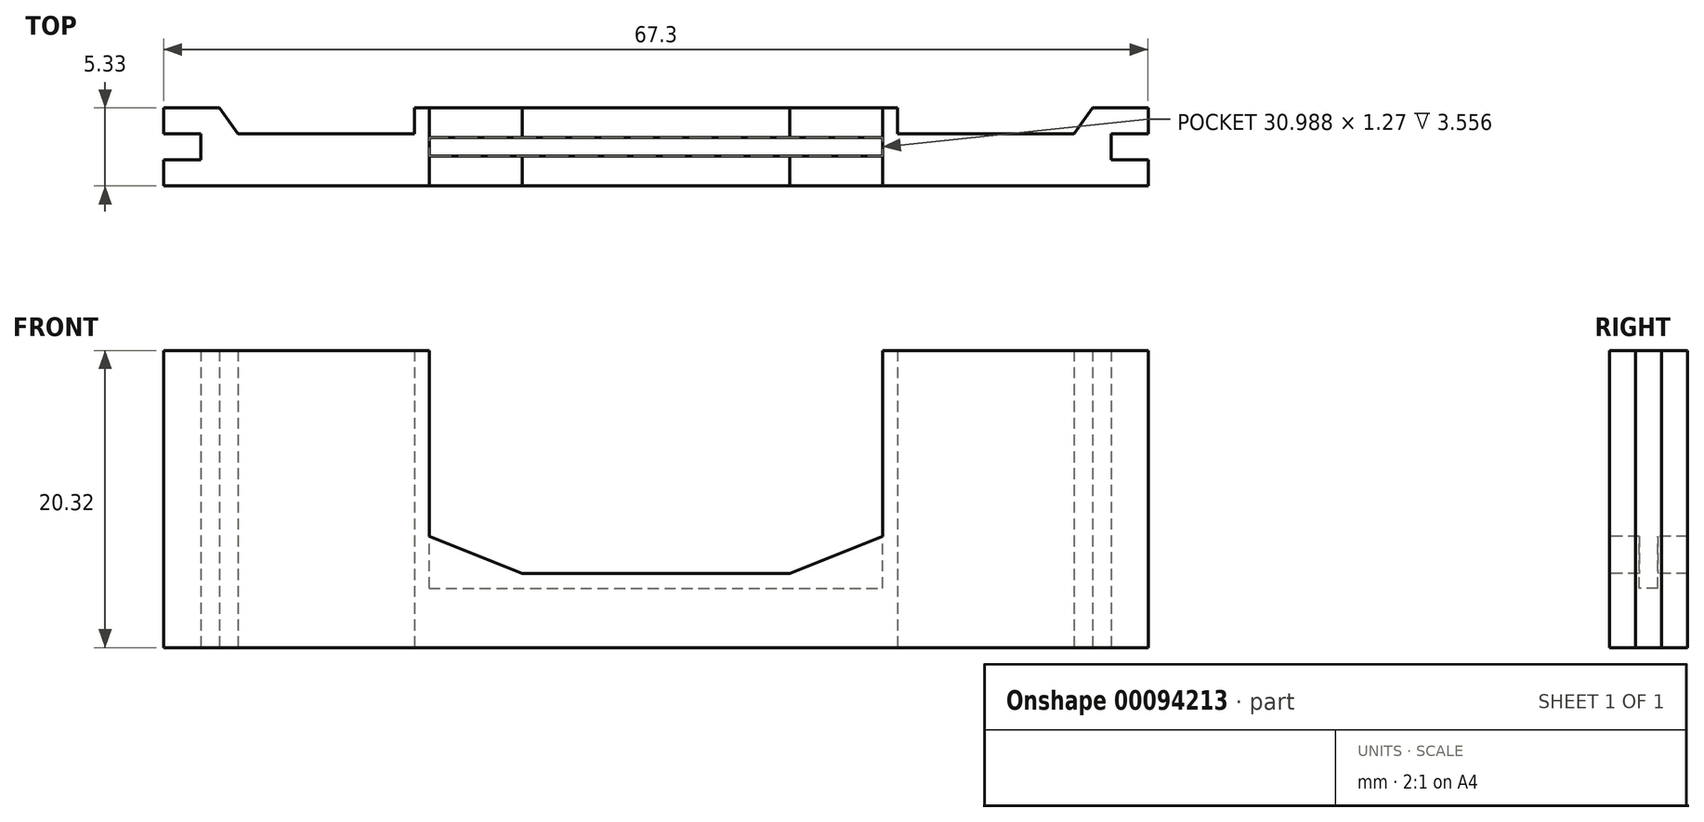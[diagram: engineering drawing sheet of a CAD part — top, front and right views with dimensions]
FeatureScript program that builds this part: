
annotation { "Feature Type Name" : "Feature", "Feature Type Description" : "" }
export const myFeature = defineFeature(function(context is Context, id is Id, definition is map)
    precondition{}
    {
        {
            var Q0;
            Q0=qCreatedBy(makeId("Top.planeOp"),FACE);
            var sketch = newSketch(context, id + "F0", { "sketchPlane" : qUnion([Q0])});
            skLineSegment(sketch, "E0", {"start": v(-33.66, 1.78) * mm, "end": v(-31.12, 1.78) * mm});
            skLineSegment(sketch, "E1", {"start": v(-31.12, 1.78) * mm, "end": v(-31.12, 3.56) * mm});
            skLineSegment(sketch, "E2", {"start": v(-31.12, 3.56) * mm, "end": v(-33.66, 3.56) * mm});
            skLineSegment(sketch, "E3", {"start": v(-33.66, 3.56) * mm, "end": v(-33.66, 5.33) * mm});
            skLineSegment(sketch, "E4", {"start": v(-33.66, 5.33) * mm, "end": v(-29.85, 5.33) * mm});
            skLineSegment(sketch, "E5", {"start": v(-16.51, 3.56) * mm, "end": v(-16.51, 5.33) * mm});
            skLineSegment(sketch, "E6", {"start": v(-16.51, 5.33) * mm, "end": v(16.51, 5.33) * mm});
            skLineSegment(sketch, "E7", {"start": v(16.5, 5.33) * mm, "end": v(16.5, 3.56) * mm});
            skLineSegment(sketch, "E8", {"start": v(29.85, 5.33) * mm, "end": v(33.66, 5.33) * mm});
            skLineSegment(sketch, "E9", {"start": v(33.66, 5.33) * mm, "end": v(33.66, 3.56) * mm});
            skLineSegment(sketch, "E10", {"start": v(33.66, 3.56) * mm, "end": v(31.12, 3.56) * mm});
            skLineSegment(sketch, "E11", {"start": v(31.12, 3.56) * mm, "end": v(31.12, 1.78) * mm});
            skLineSegment(sketch, "E12", {"start": v(31.12, 1.78) * mm, "end": v(33.66, 1.78) * mm});
            skLineSegment(sketch, "E13", {"start": v(33.66, 1.78) * mm, "end": v(33.66, 0) * mm});
            skLineSegment(sketch, "E14", {"start": v(33.66, 0) * mm, "end": v(-33.66, 0) * mm});
            skLineSegment(sketch, "E15", {"start": v(-33.66, 0) * mm, "end": v(-33.66, 1.78) * mm});
            skPoint(sketch, "E16", {"position": v(0, 5.33) * mm});
            skLineSegment(sketch, "E17", {"start": v(-29.84, 5.33) * mm, "end": v(-28.57, 3.56) * mm});
            skLineSegment(sketch, "E18", {"start": v(-28.58, 3.56) * mm, "end": v(-16.51, 3.56) * mm});
            skLineSegment(sketch, "E19", {"start": v(16.51, 3.56) * mm, "end": v(28.58, 3.56) * mm});
            skLineSegment(sketch, "E20", {"start": v(28.57, 3.56) * mm, "end": v(29.84, 5.33) * mm});
            skSolve(sketch);
        }
        {
            var Q0;
            Q0 = qSketchRegion(id + "F0", true);
            extrude(context, id + "F1", {"entities" : qUnion([Q0]), "depth" : 20.32 * mm});
        }
        {
            var Q0;
            Q0=makeQuery(id+"F1.opExtrude","CAP_FACE",FACE,{"disambiguationData":[OSD([sQuery(id+"F0.wireOp",EDGE,"E0"),sQuery(id+"F0.wireOp",EDGE,"E1"),sQuery(id+"F0.wireOp",EDGE,"E2"),sQuery(id+"F0.wireOp",EDGE,"E3"),sQuery(id+"F0.wireOp",EDGE,"E4"),sQuery(id+"F0.wireOp",EDGE,"tT2xr3kK-KxPK-BLqu-vToO-9H1Yti1pFZg4"),sQuery(id+"F0.wireOp",EDGE,"JQg3cXBy-DmHk-SCqz-GPyz-duZZdA34ewo1"),sQuery(id+"F0.wireOp",EDGE,"E5"),sQuery(id+"F0.wireOp",EDGE,"E6"),sQuery(id+"F0.wireOp",EDGE,"E7"),sQuery(id+"F0.wireOp",EDGE,"vwzpiaa3-J00z-7qOF-7MT1-leQfZo8TJBdC"),sQuery(id+"F0.wireOp",EDGE,"KlP8BnJW-x5eD-LSqO-fODY-9EMD2KD33JOl"),sQuery(id+"F0.wireOp",EDGE,"E8"),sQuery(id+"F0.wireOp",EDGE,"E9"),sQuery(id+"F0.wireOp",EDGE,"E10"),sQuery(id+"F0.wireOp",EDGE,"E11"),sQuery(id+"F0.wireOp",EDGE,"E12"),sQuery(id+"F0.wireOp",EDGE,"E13"),sQuery(id+"F0.wireOp",EDGE,"E14"),sQuery(id+"F0.wireOp",EDGE,"E15")])],"isStart":false});
            var sketch = newSketch(context, id + "F2", { "sketchPlane" : qUnion([Q0])});
            skLineSegment(sketch, "E21.bottom", {"start": v(-15.5, 5.33) * mm, "end": v(15.5, 5.33) * mm});
            skLineSegment(sketch, "E21.top", {"start": v(-15.5, 0) * mm, "end": v(15.5, 0) * mm});
            skLineSegment(sketch, "E21.left", {"start": v(-15.5, 5.33) * mm, "end": v(-15.5, 0) * mm});
            skLineSegment(sketch, "E21.right", {"start": v(15.5, 5.33) * mm, "end": v(15.5, 0) * mm});
            skPoint(sketch, "E22", {"position": v(0, 5.33) * mm});
            skSolve(sketch);
        }
        {
            var Q0;
            Q0 = qSketchRegion(id + "F2", true);
            extrude(context, id + "F3", {"entities" : qUnion([Q0]), "operationType" : NewBodyOperationType.REMOVE, "oppositeDirection" : true, "depth" : 12.7 * mm});
        }
        {
            var Q0;
            Q0=makeQuery(id+"F3.boolean.opBoolean","COPY",FACE,{"derivedFrom":makeQuery(id+"F3.opExtrude","CAP_FACE",FACE,{"disambiguationData":[OSD([sQuery(id+"F2.wireOp",EDGE,"E21.bottom"),sQuery(id+"F2.wireOp",EDGE,"E21.top"),sQuery(id+"F2.wireOp",EDGE,"E21.left"),sQuery(id+"F2.wireOp",EDGE,"E21.right")])],"isStart":false})});
            var sketch = newSketch(context, id + "F4", { "sketchPlane" : qUnion([Q0])});
            skLineSegment(sketch, "E23.bottom", {"start": v(-15.5, 3.3) * mm, "end": v(15.5, 3.3) * mm});
            skLineSegment(sketch, "E23.top", {"start": v(-15.5, 2.03) * mm, "end": v(15.5, 2.03) * mm});
            skLineSegment(sketch, "E23.left", {"start": v(-15.5, 3.3) * mm, "end": v(-15.5, 2.03) * mm});
            skLineSegment(sketch, "E23.right", {"start": v(15.5, 3.3) * mm, "end": v(15.5, 2.03) * mm});
            skPoint(sketch, "E24", {"position": v(-15.5, 2.67) * mm});
            skSolve(sketch);
        }
        {
            var Q0;
            Q0 = qSketchRegion(id + "F4", true);
            extrude(context, id + "F5", {"entities" : qUnion([Q0]), "operationType" : NewBodyOperationType.REMOVE, "oppositeDirection" : true, "depth" : 3.56 * mm});
        }
        {
            var Q0;
            Q0=makeQuery(id+"F1.opExtrude","SWEPT_FACE",FACE,{"disambiguationData":[OSD([sQuery(id+"F0.wireOp",EDGE,"E14")])]});
            var sketch = newSketch(context, id + "F6", { "sketchPlane" : qUnion([Q0])});
            skPoint(sketch, "E25", {"position": v(0, 4.06) * mm});
            skLineSegment(sketch, "E26", {"start": v(-15.5, 7.62) * mm, "end": v(-9.14, 5.08) * mm});
            skLineSegment(sketch, "E27", {"start": v(-9.14, 5.08) * mm, "end": v(9.14, 5.08) * mm});
            skLineSegment(sketch, "E28", {"start": v(9.14, 5.08) * mm, "end": v(15.5, 7.62) * mm});
            skLineSegment(sketch, "E29", {"start": v(15.5, 7.62) * mm, "end": v(-15.5, 7.62) * mm});
            skPoint(sketch, "E30", {"position": v(0, 5.08) * mm});
            skSolve(sketch);
        }
        {
            var Q0;
            Q0 = qSketchRegion(id + "F6", true);
            var Q1;
            Q1=makeQuery(id+"F1.opExtrude","SWEPT_FACE",FACE,{"disambiguationData":[OSD([sQuery(id+"F0.wireOp",EDGE,"E6")])]});
            extrude(context, id + "F7", {"entities" : qUnion([Q0]), "operationType" : NewBodyOperationType.REMOVE, "endBound" : BoundingType.UP_TO_SURFACE, "oppositeDirection" : true, "endBoundEntityFace" : qUnion([Q1]), "depth" : 25.4 * mm});
        }
    });
